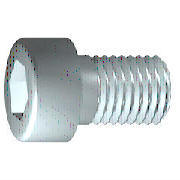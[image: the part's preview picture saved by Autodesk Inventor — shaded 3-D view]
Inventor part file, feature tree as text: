
AUTODESK INVENTOR PART (.ipt)
format: ipt  version: 2019 (Build 230136000, 136)  size: 192,000 bytes
history: native  units: mm (DEFAULTED — no unit token found)
features: sketch x2, extrude x1, plane x1, fillet x1
ambient origin geometry x7: Origin, YZ Plane, XY Plane, X Axis, Y Axis, Z Axis, Center Point
bodies: Solid1 (feature_tree), Body (feature_tree)
feature tree (5):
  extrude  "Slot"  Depth=4.0mm
  plane  "Work Plane1"
  fillet  "Fillet2"  Radius=4.0mm
  sketch  "Sketch1"  dims[d1=18.25mm d2=0.429515mm d3=4.0mm]
  sketch  "Sketch2"  dims[d4=2.0mm d5=60.0deg d6=4.0mm d7=4.0mm d8=3.464102mm d9=7.0mm d10=90.0deg d11=10.0mm d12=0.0mm d13=18.25mm d14=0.0mm d15=0.429415mm d16=0.429415mm d17=0.4mm d19=0.0mm d26=20.0mm d27=45.0deg d28=0.0mm d29=0.0mm d30=0.2mm]
